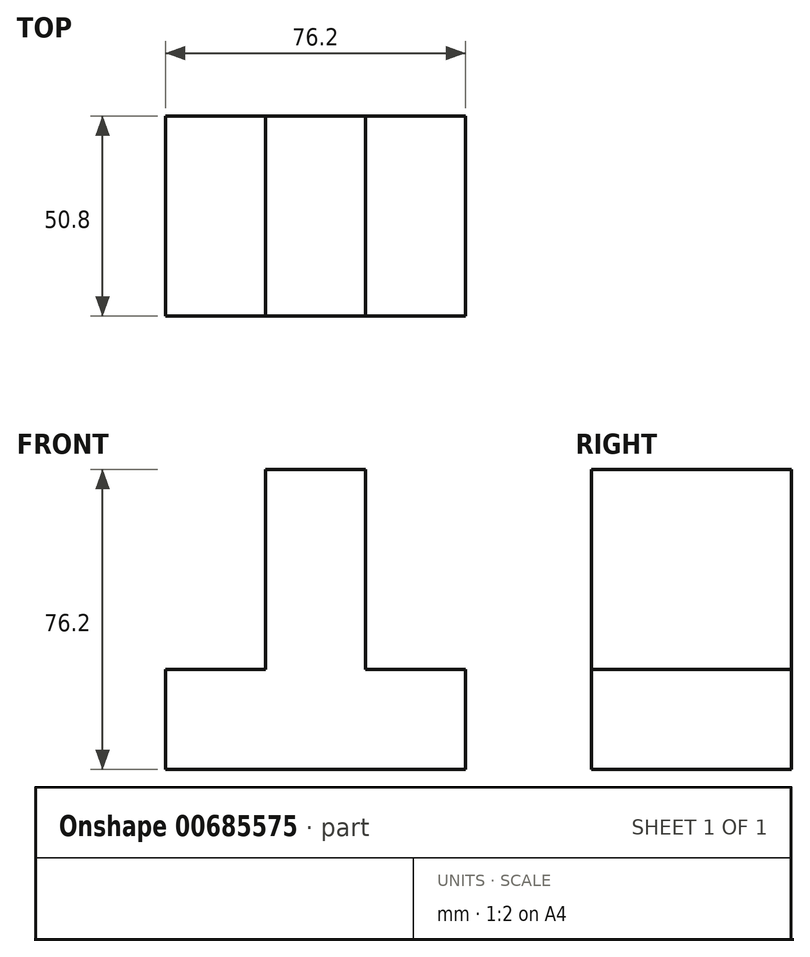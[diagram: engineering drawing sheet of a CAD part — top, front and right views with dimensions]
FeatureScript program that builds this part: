
annotation { "Feature Type Name" : "Feature", "Feature Type Description" : "" }
export const myFeature = defineFeature(function(context is Context, id is Id, definition is map)
    precondition{}
    {
        {
            var Q0;
            Q0=qCreatedBy(makeId("Front.planeOp"),FACE);
            var sketch = newSketch(context, id + "F0", { "sketchPlane" : qUnion([Q0])});
            skLineSegment(sketch, "E0", {"start": v(-18.6, 65.15) * mm, "end": v(-18.6, 14.35) * mm});
            skLineSegment(sketch, "E1", {"start": v(-18.6, 14.35) * mm, "end": v(-44, 14.35) * mm});
            skLineSegment(sketch, "E2", {"start": v(-44, 14.35) * mm, "end": v(-44, -11.05) * mm});
            skLineSegment(sketch, "E3", {"start": v(-44, -11.05) * mm, "end": v(32.2, -11.05) * mm});
            skLineSegment(sketch, "E4", {"start": v(32.2, -11.05) * mm, "end": v(32.2, 14.35) * mm});
            skLineSegment(sketch, "E5", {"start": v(32.2, 14.35) * mm, "end": v(6.8, 14.35) * mm});
            skLineSegment(sketch, "E6", {"start": v(6.8, 14.35) * mm, "end": v(6.8, 65.15) * mm});
            skLineSegment(sketch, "E7", {"start": v(6.8, 65.15) * mm, "end": v(-18.6, 65.15) * mm});
            skSolve(sketch);
        }
        {
            var Q0;
            Q0=makeQuery(id+"F0.imprint","IMPRINT",FACE,{"disambiguationData":[TD([[makeQuery(id+"F0.imprint","IMPRINT",EDGE,{"derivedFrom":sQuery(id+"F0.wireOp",EDGE,"E0")}),1.0]])]});
            extrude(context, id + "F1", {"entities" : qUnion([Q0]), "depth" : 50.8 * mm, "offsetDistance" : 25.4 * mm});
        }
    });
